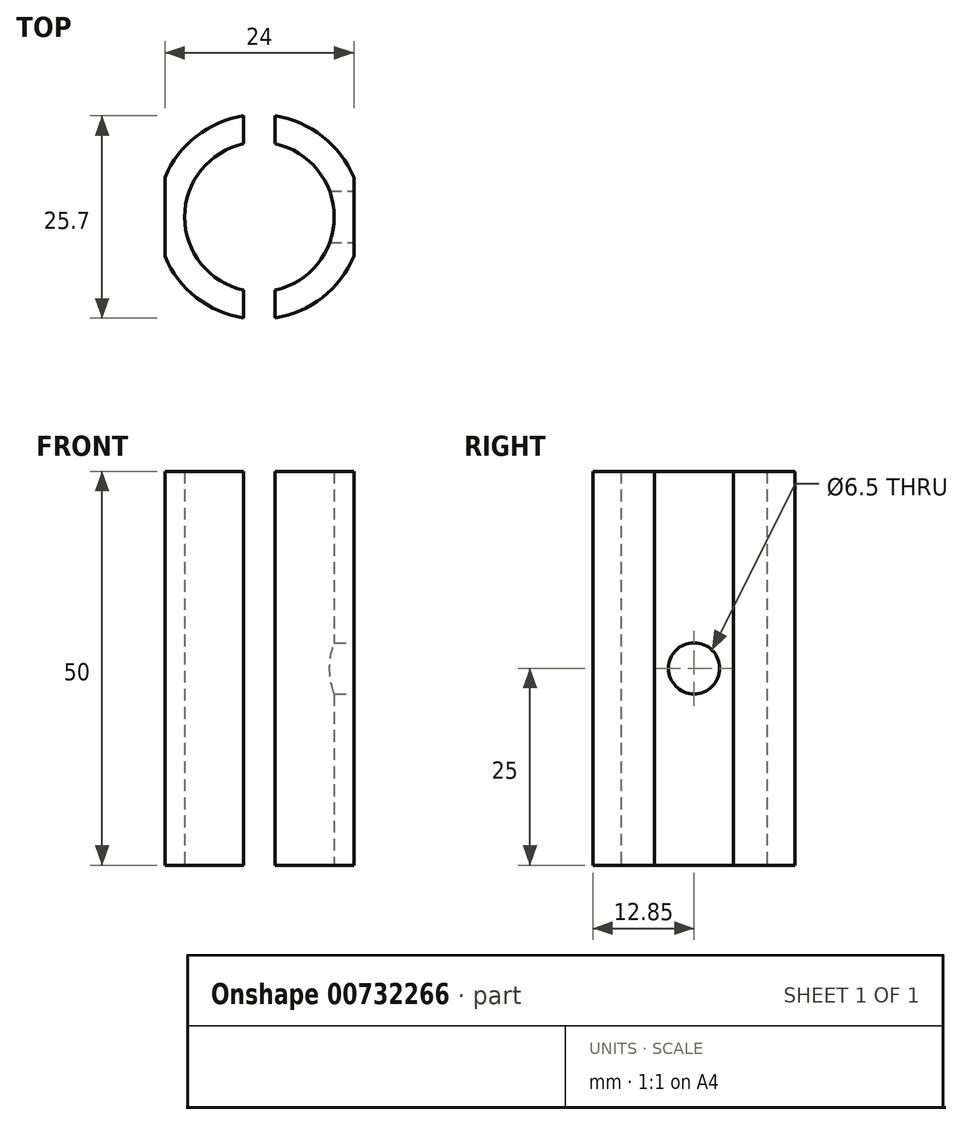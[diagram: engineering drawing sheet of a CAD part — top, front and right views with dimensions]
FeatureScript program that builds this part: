
annotation { "Feature Type Name" : "Feature", "Feature Type Description" : "" }
export const myFeature = defineFeature(function(context is Context, id is Id, definition is map)
    precondition{}
    {
        {
            var Q0;
            Q0=qCreatedBy(makeId("Top.planeOp"),FACE);
            var sketch = newSketch(context, id + "F0", { "sketchPlane" : qUnion([Q0])});
            skArc(sketch, "E0", {"start": v(12, 5) * mm, "mid": v(0, 13) * mm, "end": v(-12, 5) * mm});
            skLineSegment(sketch, "E1", {"start": v(-12, 5) * mm, "end": v(-12, -5) * mm});
            skLineSegment(sketch, "E2.MirrorCS", {"start": v(12, 5) * mm, "end": v(12, -5) * mm});
            skArc(sketch, "E3.trimOffspring", {"start": v(-12, -5) * mm, "mid": v(0, -13) * mm, "end": v(12, -5) * mm});
            skCircle(sketch, "E4", {"center": v(0, 0) * mm, "radius": 9.5 * mm});
            skLineSegment(sketch, "E5", {"start": v(0, 23.21) * mm, "end": v(0, -20.84) * mm, "construction": true});
            skLineSegment(sketch, "E6", {"start": v(-2, -9.29) * mm, "end": v(-2, -12.85) * mm});
            skLineSegment(sketch, "E7.MirrorCS", {"start": v(2, -9.29) * mm, "end": v(2, -12.85) * mm});
            skLineSegment(sketch, "E8", {"start": v(22.4, 0) * mm, "end": v(-22.98, 0) * mm, "construction": true});
            skLineSegment(sketch, "E9.MirrorCS", {"start": v(2, 9.29) * mm, "end": v(2, 12.85) * mm});
            skLineSegment(sketch, "E10.MirrorCS", {"start": v(-2, 9.29) * mm, "end": v(-2, 12.85) * mm});
            skSolve(sketch);
        }
        {
            var Q0;
            {var subQ3=sQuery(id+"F0.wireOp",EDGE,"E2.MirrorCS");Q0=makeQuery(id+"F0.imprint","IMPRINT",FACE,{"disambiguationData":[TD([[makeQuery(id+"F0.imprint","IMPRINT",EDGE,{"derivedFrom":subQ3}),-1.0]])]});}
            var Q1;
            {var subQ4=sQuery(id+"F0.wireOp",EDGE,"E1");Q1=makeQuery(id+"F0.imprint","IMPRINT",FACE,{"disambiguationData":[TD([[makeQuery(id+"F0.imprint","IMPRINT",EDGE,{"derivedFrom":subQ4}),1.0]])]});}
            extrude(context, id + "F1", {"entities" : qUnion([Q0, Q1]), "depth" : 50 * mm, "offsetDistance" : 25 * mm});
        }
        {
            var Q0;
            Q0=makeQuery(id+"F1.opExtrude","SWEPT_FACE",FACE,{"disambiguationData":[OSD([sQuery(id+"F0.wireOp",EDGE,"E2.MirrorCS")])]});
            var sketch = newSketch(context, id + "F2", { "sketchPlane" : qUnion([Q0])});
            skPoint(sketch, "E11.centerSnap0", {"position": v(5, 25) * mm});
            skPoint(sketch, "E12", {"position": v(0, 25) * mm});
            skSolve(sketch);
        }
        {
            var Q0;
            Q0=sQuery(id+"F2.wireOp",VERTEX,"E12");
            var Q1;
            Q1=makeQuery(id+"F1.opExtrude","SWEPT_BODY",BODY,{"disambiguationData":[OSD([sQuery(id+"F0.wireOp",EDGE,"E0"),sQuery(id+"F0.wireOp",EDGE,"E1"),sQuery(id+"F0.wireOp",EDGE,"E2.MirrorCS"),sQuery(id+"F0.wireOp",EDGE,"E3.trimOffspring"),sQuery(id+"F0.wireOp",EDGE,"E4"),sQuery(id+"F0.wireOp",EDGE,"E6"),sQuery(id+"F0.wireOp",EDGE,"E7.MirrorCS")])]});
            hole(context, id + "F3", {"style" : HoleStyle.SIMPLE, "endStyle" : HoleEndStyle.BLIND, "holeDiameter" : 6.5 * mm, "majorDiameter" : 5 * mm, "holeDepth" : 10 * mm, "isTappedThrough" : true, "tappedDepth" : 8 * mm, "tapClearance" : 3, "startFromSketch" : true, "locations" : qUnion([Q0]), "scope" : qUnion([Q1])});
        }
    });
